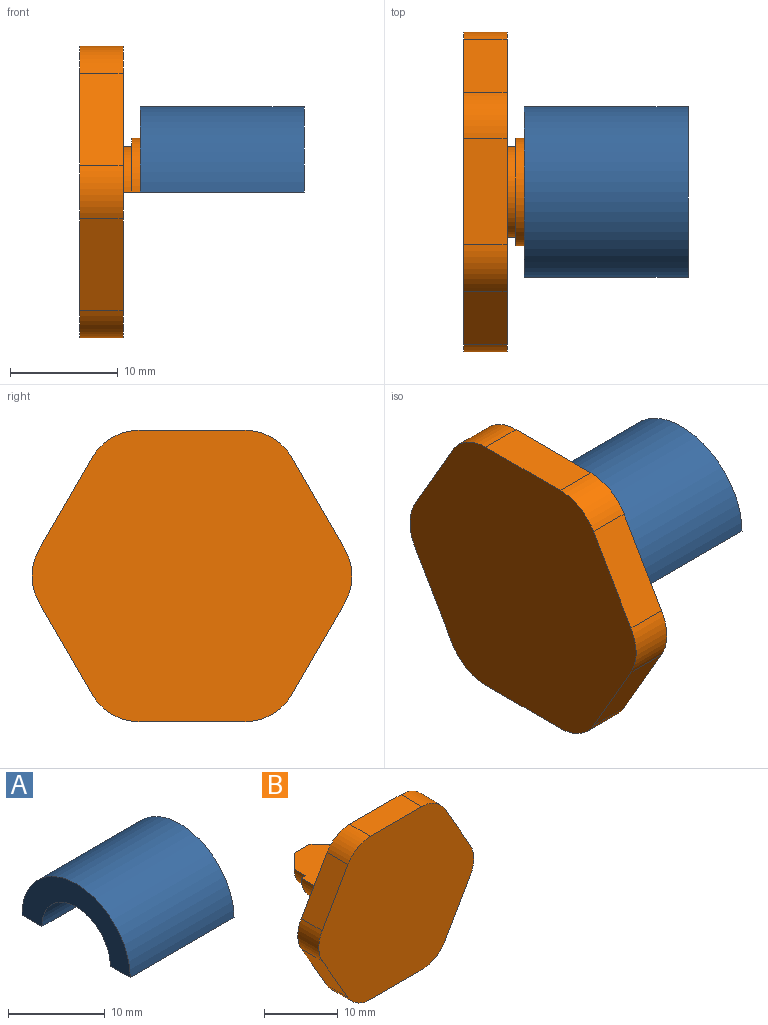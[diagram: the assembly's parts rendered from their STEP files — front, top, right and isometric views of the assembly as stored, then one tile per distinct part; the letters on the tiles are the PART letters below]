
ASSEMBLY  parts=2 mates=1
PART A: 9 faces, bbox 15.2x15.8x7.9 mm
  f0: plane 15.82x7.91mm, normal (-1,0,0), area 59mm2, adj f1,f5,f6,f7
  f1: cylinder r=5mm len=10.2mm, axis (-1,0,0), area 160.2mm2, adj f0,f2,f6,f7
  f2: cone r=5mm half-angle=60deg, axis (-1,0,0), area 38.6mm2, adj f1,f6,f7,f8
  f3: cylinder r=1.57mm len=3.15mm, axis (-1,0,0), area 14.1mm2, adj f4,f6,f7,f8
  f4: plane 15.82x7.91mm, normal (1,0,0), area 94.4mm2, adj f3,f5,f6,f7
  f5: cylinder r=7.91mm len=15.82mm, axis (-1,0,0), area 377.2mm2, adj f0,f4,f6,f7
  f6: plane 15.18x6.34mm, normal (0,0,-1), area 57.8mm2, adj f0,f1,f2,f3,f4,f5,f8
  f7: plane 15.18x6.34mm, normal (0,0,-1), area 57.8mm2, adj f0,f1,f2,f3,f4,f5,f8
  f8: cone r=1.57mm half-angle=45deg, axis (-1,0,0), area 2.8mm2, adj f2,f3,f6,f7
PART B: 22 faces, bbox 29.6x18x27 mm
  f0: plane 29.63x27mm, normal (0,1,0), area 595.9mm2, adj f1,f2,f3,f4,f5,f6,f7,f8
  f1: plane 8.5x4.91mm, normal (0.87,0,0.5), area 39.3mm2, adj f0,f2,f12,f13
  f2: cylinder r=5mm len=4.33mm, axis (0,1,0), area 20.9mm2, adj f0,f1,f3,f13
  f3: plane 9.82x4mm, normal (0,0,1), area 39.3mm2, adj f0,f2,f4,f13
  f4: cylinder r=5mm len=4.33mm, axis (0,1,0), area 20.9mm2, adj f0,f3,f5,f13
  f5: plane 8.5x4.91mm, normal (-0.87,0,0.5), area 39.3mm2, adj f0,f4,f6,f13
  f6: cylinder r=5mm len=5mm, axis (0,1,0), area 20.9mm2, adj f0,f5,f7,f13
  f7: plane 8.5x4.91mm, normal (-0.87,0,-0.5), area 39.3mm2, adj f0,f6,f8,f13
  f8: cylinder r=5mm len=4.33mm, axis (0,1,0), area 20.9mm2, adj f0,f7,f9,f13
  f9: plane 9.82x4mm, normal (0,0,-1), area 39.3mm2, adj f0,f8,f10,f13
  f10: cylinder r=5mm len=4.33mm, axis (0,1,0), area 20.9mm2, adj f0,f9,f11,f13
  f11: plane 8.5x4.91mm, normal (0.87,0,-0.5), area 39.3mm2, adj f0,f10,f12,f13
  f12: cylinder r=5mm len=5mm, axis (0,1,0), area 20.9mm2, adj f0,f1,f11,f13
  f13: plane 29.63x27mm, normal (0,-1,0), area 623.3mm2, adj f1,f2,f3,f4,f5,f6,f7,f8
  f14: cylinder r=4.17mm len=8.35mm, axis (0,1,0), area 27.9mm2, adj f15,f20,f21
  f15: plane 9.95x4.98mm, normal (0,1,0), area 11.5mm2, adj f14,f16,f21
  f16: cylinder r=4.98mm len=9.95mm, axis (0,1,0), area 131.3mm2, adj f15,f17,f21
  f17: plane 9.95x4.98mm, normal (0,-1,0), area 11.5mm2, adj f16,f18,f21
  f18: cylinder r=4.17mm len=8.35mm, axis (0,1,0), area 10.5mm2, adj f0,f17,f21
  f19: plane 3x1.5mm, normal (0,1,0), area 3.5mm2, adj f20,f21
  f20: cone r=4.17mm half-angle=45deg, axis (0,-1,0), area 33.7mm2, adj f14,f19,f21
  f21: plane 14x9.95mm, normal (0,0,1), area 123.2mm2, adj f0,f14,f15,f16,f17,f18,f19,f20
PLACE A t=(7.59,-0.52,-3.4)mm
PLACE B rot(axis=(-0.71,-0.71,0),180deg) t=(-9.19,-0.52,-3.4)mm
MATE slider B.f14 <-> A.f1  axis (1,0,0) through (-4.19,-0.52,-3.4)mm
